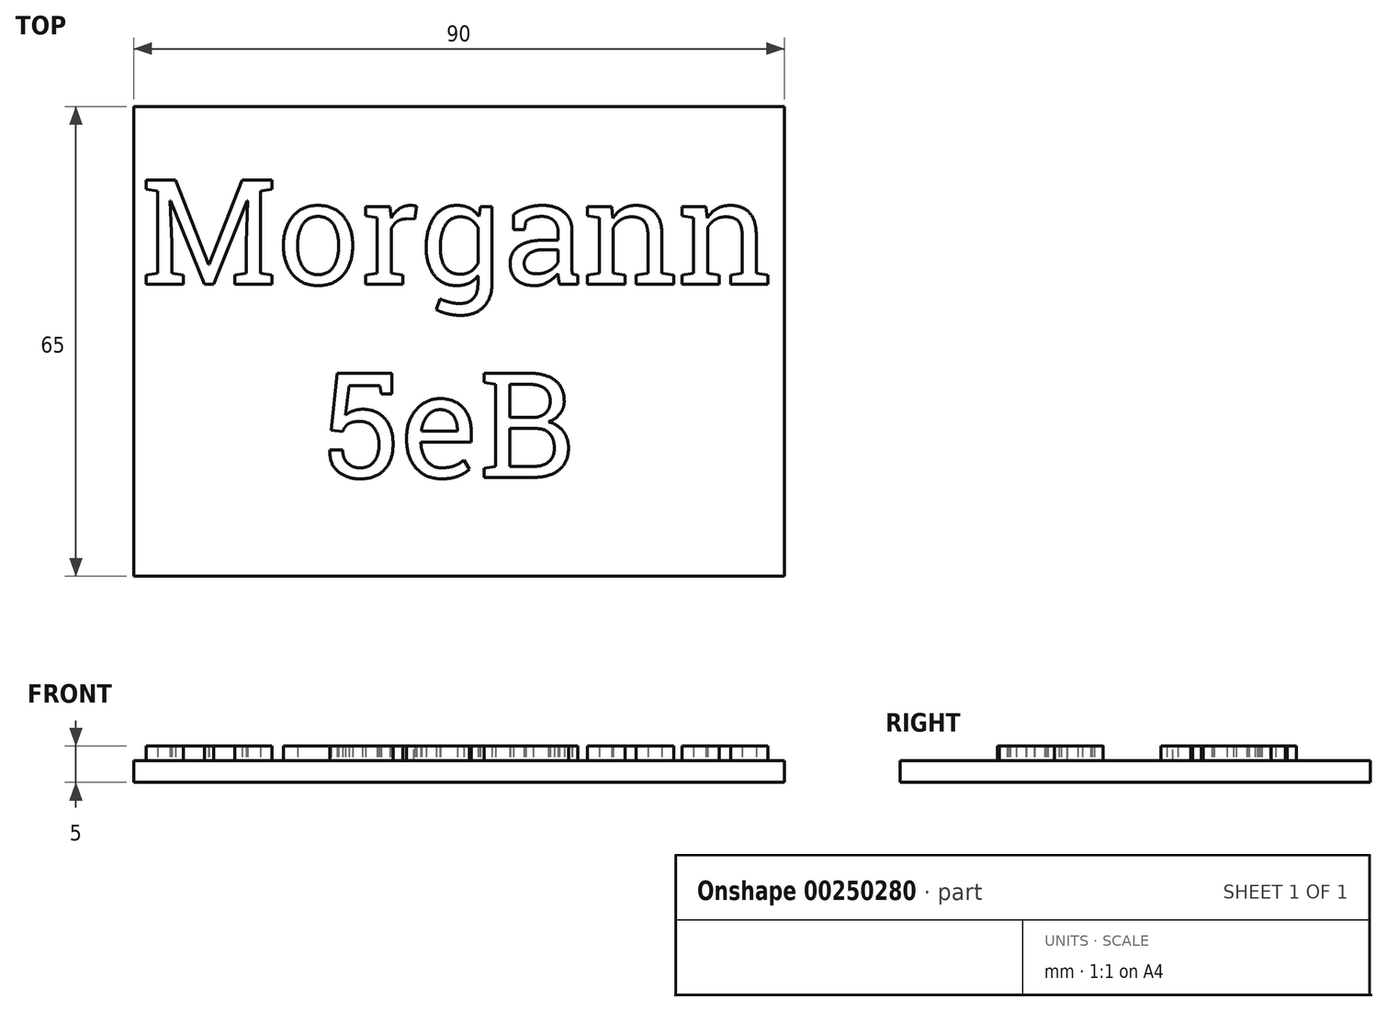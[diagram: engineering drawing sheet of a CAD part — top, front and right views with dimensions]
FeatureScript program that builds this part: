
annotation { "Feature Type Name" : "Feature", "Feature Type Description" : "" }
export const myFeature = defineFeature(function(context is Context, id is Id, definition is map)
    precondition{}
    {
        {
            var Q0;
            Q0=qCreatedBy(makeId("Top.planeOp"),FACE);
            var sketch = newSketch(context, id + "F0", { "sketchPlane" : qUnion([Q0])});
            skLineSegment(sketch, "E0.bottom", {"start": v(0, 0) * mm, "end": v(90, 0) * mm});
            skLineSegment(sketch, "E0.top", {"start": v(0, -65) * mm, "end": v(90, -65) * mm});
            skLineSegment(sketch, "E0.left", {"start": v(0, 0) * mm, "end": v(0, -65) * mm});
            skLineSegment(sketch, "E0.right", {"start": v(90, 0) * mm, "end": v(90, -65) * mm});
            skSolve(sketch);
        }
        {
            var Q0;
            Q0=makeQuery(id+"F0.imprint","IMPRINT",FACE,{"disambiguationData":[TD([[makeQuery(id+"F0.imprint","IMPRINT",EDGE,{"derivedFrom":sQuery(id+"F0.wireOp",EDGE,"E0.bottom")}),-1.0]])]});
            extrude(context, id + "F1", {"entities" : qUnion([Q0]), "depth" : 3 * mm});
        }
        {
            var Q0;
            Q0=makeQuery(id+"F1.opExtrude","CAP_FACE",FACE,{"disambiguationData":[OSD([sQuery(id+"F0.wireOp",EDGE,"E0.bottom"),sQuery(id+"F0.wireOp",EDGE,"E0.top"),sQuery(id+"F0.wireOp",EDGE,"E0.left"),sQuery(id+"F0.wireOp",EDGE,"E0.right")])],"isStart":false});
            var sketch = newSketch(context, id + "F2", { "sketchPlane" : qUnion([Q0])});
            skText(sketch, "E1", { "text": "Morgann\n     5eB", "fontName": "RobotoSlab-Regular.ttf"});
            const initialGuessF2  = {"E1": [0.001, -0.02458, 1, 0, 0.01458]};
            skSetInitialGuess(sketch, initialGuessF2);
            skSolve(sketch);
        }
        {
            var Q0;
            Q0 = qSketchRegion(id + "F2", true);
            extrude(context, id + "F3", {"entities" : qUnion([Q0]), "operationType" : NewBodyOperationType.ADD, "depth" : 2 * mm});
        }
    });
